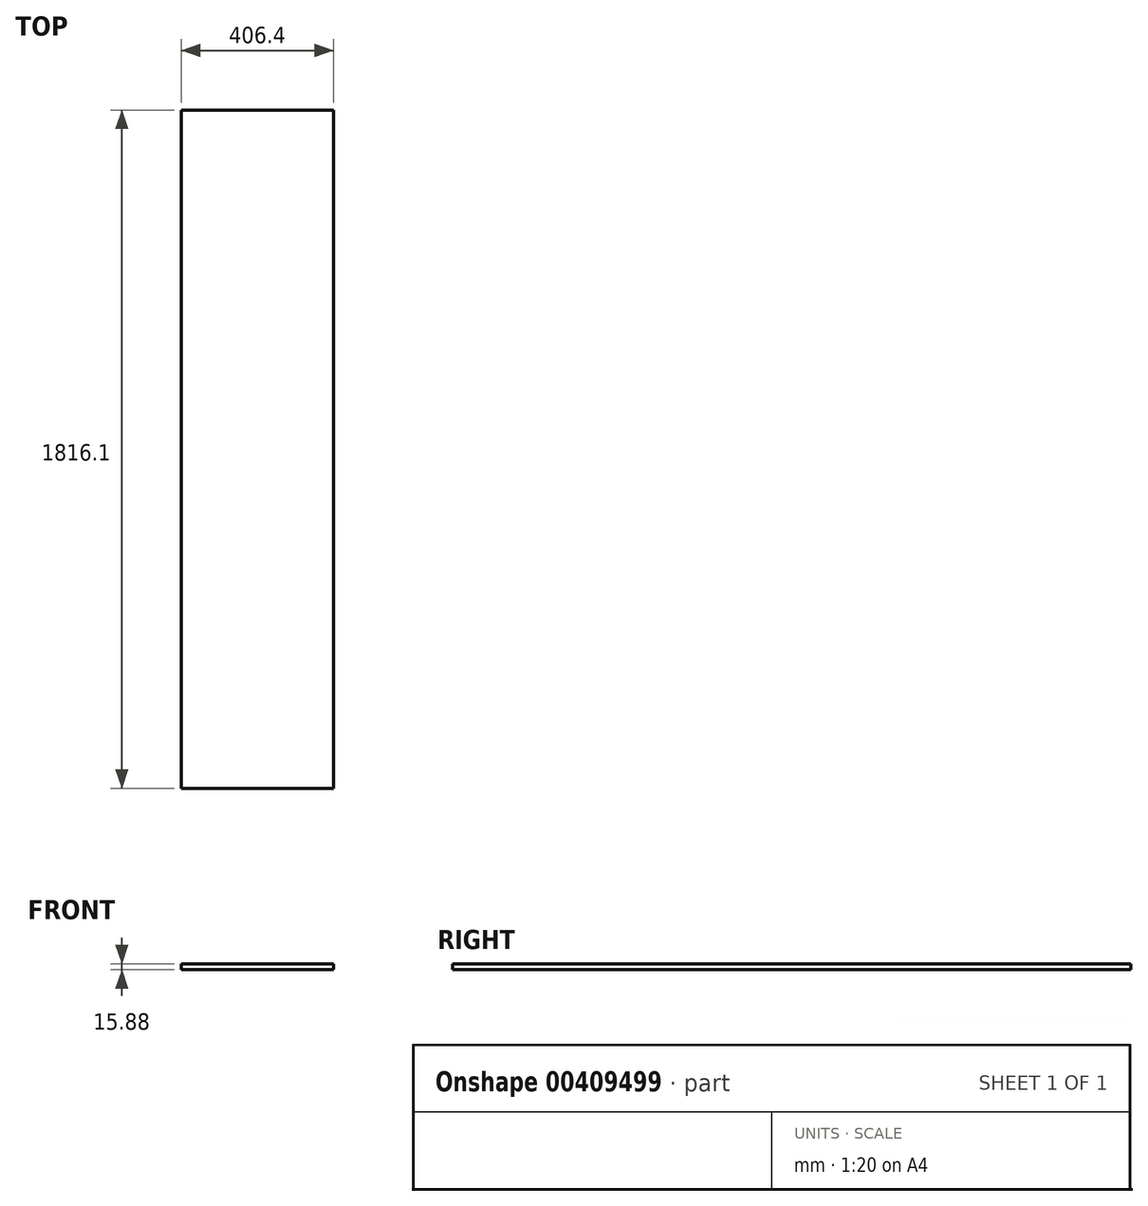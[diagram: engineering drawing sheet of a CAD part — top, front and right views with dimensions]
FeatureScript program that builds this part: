
annotation { "Feature Type Name" : "Feature", "Feature Type Description" : "" }
export const myFeature = defineFeature(function(context is Context, id is Id, definition is map)
    precondition{}
    {
        {
            var Q0;
            Q0=qCreatedBy(makeId("Front.planeOp"),FACE);
            var sketch = newSketch(context, id + "F0", { "sketchPlane" : qUnion([Q0])});
            skLineSegment(sketch, "E0.bottom", {"start": v(0, 0) * mm, "end": v(406.4, 0) * mm});
            skLineSegment(sketch, "E0.top", {"start": v(0, 15.87) * mm, "end": v(406.4, 15.87) * mm});
            skLineSegment(sketch, "E0.left", {"start": v(0, 0) * mm, "end": v(0, 15.87) * mm});
            skLineSegment(sketch, "E0.right", {"start": v(406.4, 0) * mm, "end": v(406.4, 15.87) * mm});
            skSolve(sketch);
        }
        {
            var Q0;
            Q0=makeQuery(id+"F0.imprint","IMPRINT",FACE,{"disambiguationData":[TD([[makeQuery(id+"F0.imprint","IMPRINT",EDGE,{"derivedFrom":sQuery(id+"F0.wireOp",EDGE,"E0.bottom")}),1.0]])]});
            extrude(context, id + "F1", {"entities" : qUnion([Q0]), "depth" : 1816.1 * mm});
        }
    });
